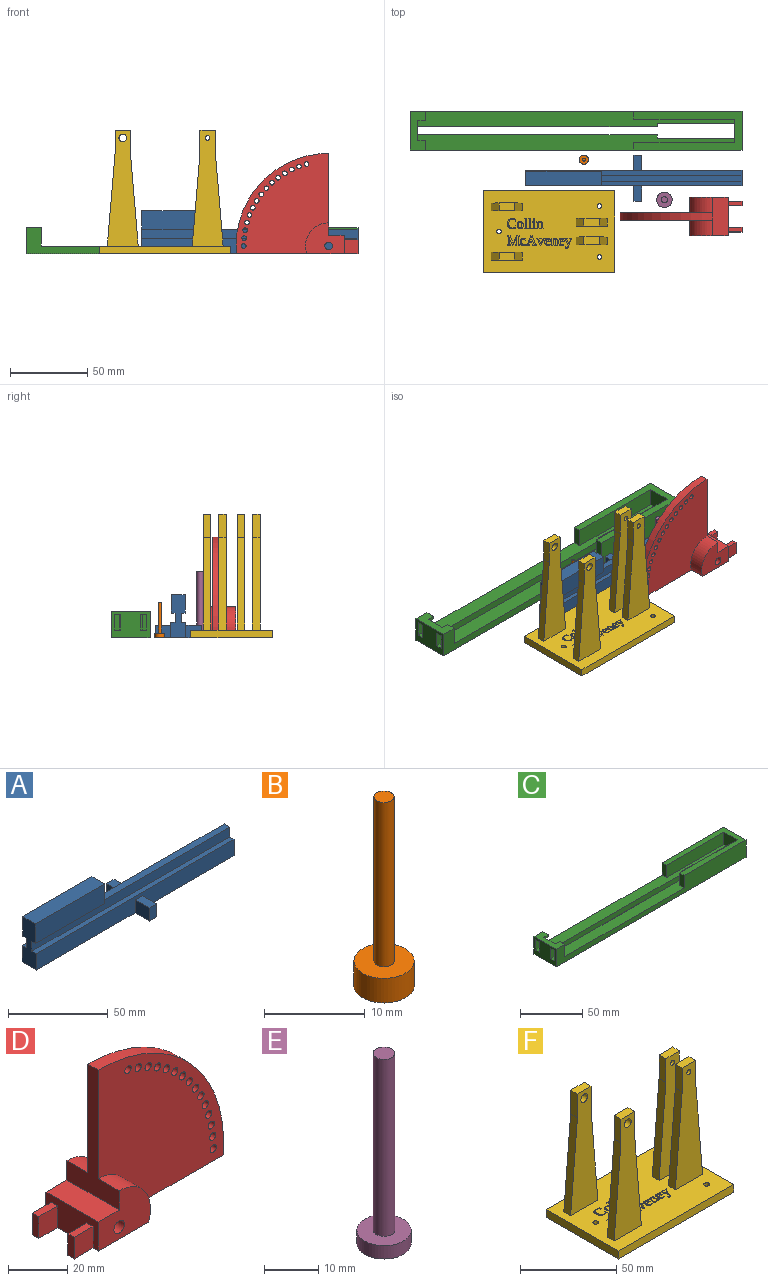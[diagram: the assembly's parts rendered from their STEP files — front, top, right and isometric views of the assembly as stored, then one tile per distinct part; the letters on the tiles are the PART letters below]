
ASSEMBLY  parts=6 mates=7
PART A: 28 faces, bbox 140x30x28 mm
  f0: plane 91x4mm, normal (0,0,1), area 364mm2, adj f11,f20,f21,f23
  f1: plane 140x3mm, normal (0,0,1), area 420mm2, adj f7,f11,f16,f21
  f2: plane 10x5.1mm, normal (0,0,1), area 51mm2, adj f4,f5,f6,f7
  f3: plane 10x5.1mm, normal (0,0,1), area 51mm2, adj f12,f13,f14,f15
  f4: plane 10x8mm, normal (-1,0,0), area 80mm2, adj f2,f5,f7,f17
  f5: plane 8x5.1mm, normal (0,-1,0), area 40.8mm2, adj f2,f4,f6,f17
  f6: plane 10x8mm, normal (1,0,0), area 80mm2, adj f2,f5,f7,f17
  f7: plane 140x10mm, normal (0,-1,0), area 1359.2mm2, adj f1,f2,f4,f6,f11,f16,f17
  f8: plane 138x8mm, normal (0,1,0), area 1104mm2, adj f9,f11,f17,f19
  f9: plane 8x2mm, normal (1,0,0), area 16mm2, adj f8,f10,f17,f19
  f10: plane 138x8mm, normal (0,-1,0), area 1104mm2, adj f9,f11,f17,f19
  f11: plane 16x10mm, normal (1,0,0), area 108mm2, adj f0,f1,f7,f8,f10,f15,f17,f18
  f12: plane 10x8mm, normal (1,0,0), area 80mm2, adj f3,f13,f15,f17
  f13: plane 8x5.1mm, normal (0,1,0), area 40.8mm2, adj f3,f12,f14,f17
  f14: plane 10x8mm, normal (-1,0,0), area 80mm2, adj f3,f13,f15,f17
  f15: plane 140x10mm, normal (0,1,0), area 1359.2mm2, adj f3,f11,f12,f14,f16,f17,f18
  f16: plane 28x10mm, normal (-1,0,0), area 232mm2, adj f1,f7,f15,f17,f18,f20,f21,f22
  f17: plane 140x30mm, normal (0,0,-1), area 1226mm2, adj f4,f5,f6,f7,f8,f9,f10,f11
  f18: plane 140x3mm, normal (0,0,1), area 420mm2, adj f11,f15,f16,f20
  f19: plane 138x2mm, normal (0,0,-1), area 276mm2, adj f8,f9,f10,f11
  f20: plane 140x6mm, normal (0,1,0), area 840mm2, adj f0,f11,f16,f18,f22
  f21: plane 140x6mm, normal (0,-1,0), area 840mm2, adj f0,f1,f11,f16,f27
  f22: plane 49x2.5mm, normal (0,0,-1), area 122.5mm2, adj f16,f20,f23,f24
  f23: plane 12x9mm, normal (1,0,0), area 108mm2, adj f0,f22,f24,f25,f26,f27
  f24: plane 49x12mm, normal (0,1,0), area 588mm2, adj f16,f22,f23,f26
  f25: plane 49x12mm, normal (0,-1,0), area 588mm2, adj f16,f23,f26,f27
  f26: plane 49x9mm, normal (0,0,1), area 441mm2, adj f16,f23,f24,f25
  f27: plane 49x2.5mm, normal (0,0,-1), area 122.5mm2, adj f16,f21,f23,f25
PART B: 5 faces, bbox 6x6x23 mm
  f0: cylinder r=3mm len=6mm, axis (0,0,-1), area 56.5mm2, adj f1,f2
  f1: plane 6x6mm, normal (0,0,1), area 25.1mm2, adj f0,f3
  f2: plane 6x6mm, normal (0,0,-1), area 28.3mm2, adj f0
  f3: cylinder r=1mm len=20mm, axis (0,0,-1), area 125.7mm2, adj f1,f4
  f4: plane 2x2mm, normal (0,0,1), area 3.1mm2, adj f3
PART C: 34 faces, bbox 215x25x17 mm
  f0: plane 210x10mm, normal (0,0,1), area 1610mm2, adj f1,f2,f5,f6,f7,f13,f16,f17
  f1: plane 25x17mm, normal (-1,0,0), area 345mm2, adj f0,f4,f12,f13,f18,f21,f22,f23
  f2: plane 12x6mm, normal (1,0,0), area 32mm2, adj f0,f13,f19,f21,f26,f27
  f3: plane 12x6mm, normal (1,0,0), area 32mm2, adj f4,f12,f20,f21,f23,f24
  f4: plane 210x10mm, normal (0,0,1), area 1610mm2, adj f1,f3,f7,f8,f9,f10,f12,f16
  f5: plane 5x2.5mm, normal (1,0,0), area 12.5mm2, adj f0,f6,f17,f18
  f6: plane 155x5mm, normal (0,1,0), area 775mm2, adj f0,f5,f7,f18
  f7: plane 17x13mm, normal (1,0,0), area 181mm2, adj f0,f4,f6,f8,f18,f19,f20,f21
  f8: plane 155x5mm, normal (0,-1,0), area 775mm2, adj f4,f7,f9,f18
  f9: plane 5x2.5mm, normal (1,0,0), area 12.5mm2, adj f4,f8,f10,f18
  f10: plane 50x5mm, normal (0,-1,0), area 250mm2, adj f4,f9,f16,f18
  f11: plane 7x5mm, normal (0,-1,0), area 35mm2, adj f14,f16,f18,f33
  f12: plane 215x17mm, normal (0,1,0), area 2035mm2, adj f1,f3,f4,f14,f18,f21,f28,f32
  f13: plane 215x17mm, normal (0,-1,0), area 2035mm2, adj f0,f1,f2,f14,f18,f21,f31,f32
  f14: plane 25x17mm, normal (1,0,0), area 390mm2, adj f11,f12,f13,f15,f18,f32,f33
  f15: plane 7x5mm, normal (0,1,0), area 35mm2, adj f14,f16,f18,f33
  f16: plane 17x15mm, normal (-1,0,0), area 195mm2, adj f0,f4,f10,f11,f15,f17,f18,f29
  f17: plane 50x5mm, normal (0,1,0), area 250mm2, adj f0,f5,f16,f18
  f18: plane 215x25mm, normal (0,0,-1), area 4075mm2, adj f1,f5,f6,f7,f8,f9,f10,f11
  f19: plane 5x2mm, normal (0,1,0), area 10mm2, adj f2,f7,f21,f26
  f20: plane 5x2mm, normal (0,-1,0), area 10mm2, adj f3,f7,f21,f23
  f21: plane 25x10mm, normal (0,0,1), area 185mm2, adj f1,f2,f3,f7,f12,f13,f19,f20
  f22: plane 10x5mm, normal (0,1,0), area 50mm2, adj f1,f4,f7,f23
  f23: plane 10x4mm, normal (0,0,-1), area 40mm2, adj f1,f3,f20,f22,f24
  f24: plane 10x10mm, normal (0,-1,0), area 100mm2, adj f1,f3,f4,f23
  f25: plane 10x5mm, normal (0,-1,0), area 50mm2, adj f0,f1,f7,f26
  f26: plane 10x4mm, normal (0,0,-1), area 40mm2, adj f1,f2,f19,f25,f27
  f27: plane 10x10mm, normal (0,1,0), area 100mm2, adj f0,f1,f2,f26
  f28: plane 12x5mm, normal (-1,0,0), area 60mm2, adj f4,f12,f29,f32
  f29: plane 65x12mm, normal (0,-1,0), area 780mm2, adj f4,f16,f28,f32
  f30: plane 65x12mm, normal (0,1,0), area 780mm2, adj f0,f16,f31,f32
  f31: plane 12x5mm, normal (-1,0,0), area 60mm2, adj f0,f13,f30,f32
  f32: plane 70x25mm, normal (0,0,1), area 775mm2, adj f12,f13,f14,f16,f28,f29,f30,f31
  f33: plane 5x5mm, normal (0,0,-1), area 25mm2, adj f11,f14,f15,f16
PART D: 35 faces, bbox 79x25x65 mm
  f0: plane 25x12mm, normal (-1,0,0), area 246mm2, adj f18,f19,f20,f22,f27,f28,f29,f31
  f1: plane 53x25mm, normal (-1,0,0), area 425mm2, adj f17,f18,f19,f22,f23,f24,f25,f26
  f2: cylinder r=1.5mm len=5mm, axis (0,1,0), area 47.1mm2, adj f24,f26
  f3: cylinder r=1.5mm len=5mm, axis (0,1,0), area 47.1mm2, adj f24,f26
  f4: cylinder r=1.5mm len=5mm, axis (0,1,0), area 47.1mm2, adj f24,f26
  f5: cylinder r=1.5mm len=5mm, axis (0,1,0), area 47.1mm2, adj f24,f26
  f6: cylinder r=1.5mm len=5mm, axis (0,1,0), area 47.1mm2, adj f24,f26
  f7: cylinder r=1.5mm len=5mm, axis (0,1,0), area 47.1mm2, adj f24,f26
  f8: cylinder r=1.5mm len=5mm, axis (0,1,0), area 47.1mm2, adj f24,f26
  f9: cylinder r=1.5mm len=5mm, axis (0,1,0), area 47.1mm2, adj f24,f26
  f10: cylinder r=1.5mm len=5mm, axis (0,1,0), area 47.1mm2, adj f24,f26
  f11: cylinder r=1.5mm len=5mm, axis (0,1,0), area 47.1mm2, adj f24,f26
  f12: cylinder r=1.5mm len=5mm, axis (0,1,0), area 47.1mm2, adj f24,f26
  f13: cylinder r=1.5mm len=5mm, axis (0,1,0), area 47.1mm2, adj f24,f26
  f14: cylinder r=1.5mm len=5mm, axis (0,1,0), area 47.1mm2, adj f24,f26
  f15: cylinder r=1.5mm len=5mm, axis (0,1,0), area 47.1mm2, adj f24,f26
  f16: cylinder r=1.5mm len=5mm, axis (0,1,0), area 47.1mm2, adj f24,f26
  f17: cylinder r=60mm len=65mm, axis (0,1,0), area 496.3mm2, adj f1,f20,f24,f26
  f18: plane 25x20mm, normal (0,-1,0), area 350.7mm2, adj f0,f1,f19,f20,f21,f23
  f19: plane 25x10mm, normal (0,0,1), area 250mm2, adj f0,f1,f18,f22
  f20: plane 78.79x25mm, normal (0,0,-1), area 885.8mm2, adj f0,f17,f18,f22,f23,f24,f25,f26
  f21: cylinder r=2.5mm len=25mm, axis (0,1,0), area 392.7mm2, adj f18,f22
  f22: plane 25x20mm, normal (0,1,0), area 350.7mm2, adj f0,f1,f19,f20,f21,f25
  f23: cylinder r=15mm len=20mm, axis (0,-1,0), area 286.6mm2, adj f1,f18,f20,f24
  f24: plane 65x60mm, normal (0,-1,0), area 2770.8mm2, adj f1,f2,f3,f4,f5,f6,f7,f8
  f25: cylinder r=15mm len=20mm, axis (0,1,0), area 286.6mm2, adj f1,f20,f22,f26
  f26: plane 65x60mm, normal (0,1,0), area 2770.8mm2, adj f1,f2,f3,f4,f5,f6,f7,f8
  f27: plane 9x3mm, normal (0,0,1), area 27mm2, adj f0,f28,f29,f30
  f28: plane 9x9mm, normal (0,1,0), area 81mm2, adj f0,f20,f27,f30
  f29: plane 9x9mm, normal (0,-1,0), area 81mm2, adj f0,f20,f27,f30
  f30: plane 9x3mm, normal (-1,0,0), area 27mm2, adj f20,f27,f28,f29
  f31: plane 9x9mm, normal (0,-1,0), area 81mm2, adj f0,f20,f32,f34
  f32: plane 9x3mm, normal (0,0,1), area 27mm2, adj f0,f31,f33,f34
  f33: plane 9x9mm, normal (0,1,0), area 81mm2, adj f0,f20,f32,f34
  f34: plane 9x3mm, normal (-1,0,0), area 27mm2, adj f20,f31,f32,f33
PART E: 5 faces, bbox 10x10x43 mm
  f0: cylinder r=5mm len=10mm, axis (0,0,-1), area 94.2mm2, adj f1,f2
  f1: plane 10x10mm, normal (0,0,1), area 66mm2, adj f0,f3
  f2: plane 10x10mm, normal (0,0,-1), area 78.5mm2, adj f0
  f3: cylinder r=2mm len=40mm, axis (0,0,-1), area 502.7mm2, adj f1,f4
  f4: plane 4x4mm, normal (0,0,1), area 12.6mm2, adj f3
PART F: 324 faces, bbox 85x53x80 mm
  f0: plane 85x53mm, normal (0,0,1), area 3956.6mm2, adj f5,f6,f7,f8,f10,f11,f13,f15
  f1: plane 15x5mm, normal (-1,0,0), area 75mm2, adj f10,f11,f12,f37
  f2: plane 15x5mm, normal (1,0,0), area 75mm2, adj f10,f11,f12,f36
  f3: plane 15x5mm, normal (-1,0,0), area 75mm2, adj f18,f19,f20,f35
  f4: plane 15x5mm, normal (1,0,0), area 75mm2, adj f18,f19,f20,f34
  f5: plane 85x5mm, normal (0,-1,0), area 425mm2, adj f0,f6,f8,f9
  f6: plane 53x5mm, normal (1,0,0), area 265mm2, adj f0,f5,f7,f9
  f7: plane 85x5mm, normal (0,1,0), area 425mm2, adj f0,f6,f8,f9
  f8: plane 53x5mm, normal (-1,0,0), area 265mm2, adj f0,f5,f7,f9
  f9: plane 85x53mm, normal (0,0,-1), area 4483.8mm2, adj f5,f6,f7,f8,f38,f39,f40
  f10: plane 75x20mm, normal (0,1,0), area 1030.4mm2, adj f0,f1,f2,f12,f29,f36,f37
  f11: plane 75x20mm, normal (0,-1,0), area 1030.4mm2, adj f0,f1,f2,f12,f29,f36,f37
  f12: plane 10x5mm, normal (0,0,1), area 50mm2, adj f1,f2,f10,f11
  f13: plane 75x20mm, normal (0,1,0), area 1030.4mm2, adj f0,f14,f16,f17,f28,f30,f31
  f14: plane 15x5mm, normal (-1,0,0), area 75mm2, adj f13,f15,f17,f30
  f15: plane 75x20mm, normal (0,-1,0), area 1030.4mm2, adj f0,f14,f16,f17,f28,f30,f31
  f16: plane 15x5mm, normal (1,0,0), area 75mm2, adj f13,f15,f17,f31
  f17: plane 10x5mm, normal (0,0,1), area 50mm2, adj f13,f14,f15,f16
  f18: plane 75x20mm, normal (0,1,0), area 1042.9mm2, adj f0,f3,f4,f20,f27,f34,f35
  f19: plane 75x20mm, normal (0,-1,0), area 1042.9mm2, adj f0,f3,f4,f20,f27,f34,f35
  f20: plane 10x5mm, normal (0,0,1), area 50mm2, adj f3,f4,f18,f19
  f21: plane 75x20mm, normal (0,1,0), area 1042.9mm2, adj f0,f22,f24,f25,f26,f32,f33
  f22: plane 15x5mm, normal (-1,0,0), area 75mm2, adj f21,f23,f25,f32
  f23: plane 75x20mm, normal (0,-1,0), area 1042.9mm2, adj f0,f22,f24,f25,f26,f32,f33
  f24: plane 15x5mm, normal (1,0,0), area 75mm2, adj f21,f23,f25,f33
  f25: plane 10x5mm, normal (0,0,1), area 50mm2, adj f21,f22,f23,f24
  f26: cylinder r=1.5mm len=5mm, axis (0,-1,0), area 47.1mm2, adj f21,f23
  f27: cylinder r=1.5mm len=5mm, axis (0,-1,0), area 47.1mm2, adj f18,f19
  f28: cylinder r=2.5mm len=5mm, axis (0,-1,0), area 78.5mm2, adj f13,f15
  f29: cylinder r=2.5mm len=5mm, axis (0,-1,0), area 78.5mm2, adj f10,f11
  f30: plane 60x5mm, normal (-1,0,0.08), area 301mm2, adj f0,f13,f14,f15
  f31: plane 60x5mm, normal (1,0,0.08), area 301mm2, adj f0,f13,f15,f16
  f32: plane 60x5mm, normal (-1,0,0.08), area 301mm2, adj f0,f21,f22,f23
  f33: plane 60x5mm, normal (1,0,0.08), area 301mm2, adj f0,f21,f23,f24
  f34: plane 60x5mm, normal (1,0,0.08), area 301mm2, adj f0,f4,f18,f19
  f35: plane 60x5mm, normal (-1,0,0.08), area 301mm2, adj f0,f3,f18,f19
  f36: plane 60x5mm, normal (1,0,0.08), area 301mm2, adj f0,f2,f10,f11
  f37: plane 60x5mm, normal (-1,0,0.08), area 301mm2, adj f0,f1,f10,f11
  f38: cylinder r=1.5mm len=5mm, axis (0,0,1), area 47.1mm2, adj f0,f9
  f39: cylinder r=1.5mm len=5mm, axis (0,0,1), area 47.1mm2, adj f0,f9
  f40: cylinder r=1.5mm len=5mm, axis (0,0,1), area 47.1mm2, adj f0,f9
  f41: extruded ~2.36x2mm, area 5.1mm2, adj f0,f42,f60,f61
  f42: extruded ~2.2x2mm, area 4.5mm2, adj f0,f41,f43,f61
  f43: plane 2x1.47mm, normal (-1,0.02,0), area 2.9mm2, adj f0,f42,f44,f61
  f44: plane 2x0.3mm, normal (0,-1,0), area 0.6mm2, adj f0,f43,f45,f61
  f45: plane 2x0.93mm, normal (0.98,-0.18,0), area 1.9mm2, adj f0,f44,f46,f61
  f46: extruded ~2x0.74mm, area 1.6mm2, adj f0,f45,f47,f61
  f47: extruded ~2x1mm, area 2mm2, adj f0,f46,f48,f61
  f48: extruded ~2x1.67mm, area 3.8mm2, adj f0,f47,f49,f61
  f49: extruded ~2.07x2mm, area 4.4mm2, adj f0,f48,f50,f61
  f50: extruded ~2.18x2mm, area 4.6mm2, adj f0,f49,f51,f61
  f51: extruded ~2x1.74mm, area 3.9mm2, adj f0,f50,f52,f61
  f52: extruded ~2x0.88mm, area 1.8mm2, adj f0,f51,f53,f61
  f53: extruded ~2x0.76mm, area 1.6mm2, adj f0,f52,f54,f61
  f54: plane 2x0.81mm, normal (0.99,0.17,0), area 1.6mm2, adj f0,f53,f55,f61
  f55: plane 2x0.31mm, normal (0,1,0), area 0.6mm2, adj f0,f54,f56,f61
  f56: plane 2x1.36mm, normal (-1,-0.02,0), area 2.7mm2, adj f0,f55,f57,f61
  f57: extruded ~2.09x2mm, area 4.2mm2, adj f0,f56,f58,f61
  f58: extruded ~2.41x2mm, area 5.2mm2, adj f0,f57,f59,f61
  f59: extruded ~2.43x2mm, area 5.3mm2, adj f0,f58,f60,f61
  f60: extruded ~2.31x2mm, area 5.1mm2, adj f0,f41,f59,f61
  f61: plane 6.4x5.44mm, normal (0,0,1), area 9.1mm2, adj f41,f42,f43,f44,f45,f46,f47,f48
  f62: extruded ~2x0.76mm, area 1.7mm2, adj f0,f63,f86,f87
  f63: plane 2x0.35mm, normal (-0.99,-0.12,0), area 0.7mm2, adj f0,f62,f64,f87
  f64: plane 2x1.25mm, normal (0,-1,0), area 2.5mm2, adj f0,f63,f65,f87
  f65: plane 2x0.21mm, normal (1,0,0), area 0.4mm2, adj f0,f64,f66,f87
  f66: plane 2x0.53mm, normal (0.22,0.98,0), area 1.1mm2, adj f0,f65,f67,f87
  f67: plane 3.72x2mm, normal (1,0,0), area 7.4mm2, adj f0,f66,f68,f87
  f68: plane 2x0.53mm, normal (0.22,-0.98,0), area 1.1mm2, adj f0,f67,f69,f87
  f69: plane 2x0.21mm, normal (1,0,0), area 0.4mm2, adj f0,f68,f70,f87
  f70: plane 2x1.89mm, normal (0,1,0), area 3.8mm2, adj f0,f69,f71,f87
  f71: plane 2x0.21mm, normal (-1,0,0), area 0.4mm2, adj f0,f70,f72,f87
  f72: plane 2x0.59mm, normal (-0.19,-0.98,0), area 1.2mm2, adj f0,f71,f73,f87
  f73: plane 3.48x2mm, normal (-1,0,0), area 7mm2, adj f0,f72,f74,f87
  f74: extruded ~2x1.03mm, area 2.1mm2, adj f0,f73,f75,f87
  f75: extruded ~2x0.58mm, area 1.3mm2, adj f0,f74,f76,f87
  f76: extruded ~2x0.61mm, area 1.3mm2, adj f0,f75,f77,f87
  f77: plane 2.79x2mm, normal (1,0,0), area 5.6mm2, adj f0,f76,f78,f87
  f78: plane 2x0.58mm, normal (0.2,-0.98,0), area 1.2mm2, adj f0,f77,f79,f87
  f79: plane 2x0.21mm, normal (1,0,0), area 0.4mm2, adj f0,f78,f80,f87
  f80: plane 2x1.88mm, normal (0,1,0), area 3.8mm2, adj f0,f79,f81,f87
  f81: plane 2x0.21mm, normal (-1,0,0), area 0.4mm2, adj f0,f80,f82,f87
  f82: plane 2x0.53mm, normal (-0.21,-0.98,0), area 1.1mm2, adj f0,f81,f83,f87
  f83: plane 2.87x2mm, normal (-1,0,0), area 5.7mm2, adj f0,f82,f84,f87
  f84: extruded ~2x0.96mm, area 2mm2, adj f0,f83,f85,f87
  f85: extruded ~2x0.86mm, area 1.9mm2, adj f0,f84,f86,f87
  f86: extruded ~2x0.67mm, area 1.4mm2, adj f0,f62,f85,f87
  f87: plane 4.49x4.4mm, normal (0,0,1), area 8.2mm2, adj f62,f63,f64,f65,f66,f67,f68,f69
  f88: extruded ~2x0.72mm, area 1.4mm2, adj f0,f89,f112,f113
  f89: extruded ~2x0.62mm, area 1.3mm2, adj f0,f88,f90,f113
  f90: extruded ~2x0.51mm, area 1.4mm2, adj f0,f89,f91,f113
  f91: extruded ~2x1.1mm, area 2.4mm2, adj f0,f90,f92,f113
  f92: plane 4.34x2mm, normal (-0.93,0.37,0), area 9.3mm2, adj f0,f91,f93,f113
  f93: plane 2x0.46mm, normal (-0.21,0.98,0), area 0.9mm2, adj f0,f92,f94,f113
  f94: plane 2x0.21mm, normal (-1,0,0), area 0.4mm2, adj f0,f93,f95,f113
  f95: plane 2x1.63mm, normal (0,-1,0), area 3.3mm2, adj f0,f94,f96,f113
  f96: plane 2x0.21mm, normal (1,0,0), area 0.4mm2, adj f0,f95,f97,f113
  f97: plane 2x0.68mm, normal (0.17,0.99,0), area 1.4mm2, adj f0,f96,f98,f113
  f98: plane 3.07x2mm, normal (0.94,-0.35,0), area 6.5mm2, adj f0,f97,f99,f113
  f99: plane 3.06x2mm, normal (-0.93,-0.36,0), area 6.6mm2, adj f0,f98,f100,f113
  f100: plane 2x0.69mm, normal (-0.18,0.98,0), area 1.4mm2, adj f0,f99,f101,f113
  f101: plane 2x0.21mm, normal (-1,0,0), area 0.4mm2, adj f0,f100,f102,f113
  f102: plane 2.03x2mm, normal (0,-1,0), area 4.1mm2, adj f0,f101,f103,f113
  f103: plane 2x0.21mm, normal (1,0,0), area 0.4mm2, adj f0,f102,f104,f113
  f104: plane 2x0.45mm, normal (0.25,0.97,0), area 0.9mm2, adj f0,f103,f105,f113
  f105: plane 4.09x2mm, normal (0.93,0.38,0), area 8.8mm2, adj f0,f104,f106,f113
  f106: extruded ~2x0.98mm, area 2.1mm2, adj f0,f105,f107,f113
  f107: extruded ~2x0.41mm, area 1.1mm2, adj f0,f106,f108,f113
  f108: extruded ~2x0.45mm, area 1mm2, adj f0,f107,f109,f113
  f109: extruded ~2x0.4mm, area 0.8mm2, adj f0,f108,f110,f113
  f110: plane 2x0.45mm, normal (-0.95,-0.32,0), area 0.9mm2, adj f0,f109,f111,f113
  f111: plane 2x0.22mm, normal (0,-1,0), area 0.4mm2, adj f0,f110,f112,f113
  f112: plane 2x0.94mm, normal (1,0,0), area 1.9mm2, adj f0,f88,f111,f113
  f113: plane 6.43x4.61mm, normal (0,0,1), area 7.4mm2, adj f88,f89,f90,f91,f92,f93,f94,f95
  f114: extruded ~2x1.46mm, area 3mm2, adj f115,f128,f129,f320
  f115: extruded ~2x1.48mm, area 3.1mm2, adj f114,f116,f129,f320
  f116: extruded ~2x0.91mm, area 2.1mm2, adj f115,f117,f129,f320
  f117: extruded ~2x0.88mm, area 2.1mm2, adj f116,f118,f129,f320
  f118: extruded ~2x1.49mm, area 3.1mm2, adj f117,f119,f129,f320
  f119: extruded ~2x1.47mm, area 3mm2, adj f118,f120,f129,f320
  f120: extruded ~2x0.88mm, area 2.1mm2, adj f119,f128,f129,f320
  f121: extruded ~2.3x2.05mm, area 7.1mm2, adj f0,f122,f127,f129
  f122: extruded ~2x1.71mm, area 3.6mm2, adj f0,f121,f123,f129
  f123: extruded ~2x1.5mm, area 3.3mm2, adj f0,f122,f124,f129
  f124: extruded ~2x1.52mm, area 3.4mm2, adj f0,f123,f125,f129
  f125: extruded ~2x1.69mm, area 3.6mm2, adj f0,f124,f126,f129
  f126: extruded ~2x1.71mm, area 3.6mm2, adj f0,f125,f127,f129
  f127: extruded ~2x1.49mm, area 3.3mm2, adj f0,f121,f126,f129
  f128: extruded ~2x0.92mm, area 2.1mm2, adj f114,f120,f129,f320
  f129: plane 4.58x4.04mm, normal (0,0,1), area 7.7mm2, adj f114,f115,f116,f117,f118,f119,f120,f121
  f130: plane 3.03x2mm, normal (-0.94,0.33,0), area 6.4mm2, adj f131,f148,f149,f321
  f131: plane 3.03x2mm, normal (0.94,0.34,0), area 6.4mm2, adj f130,f148,f149,f321
  f132: plane 2x0.25mm, normal (-1,0,0), area 0.5mm2, adj f0,f133,f147,f149
  f133: plane 2x0.84mm, normal (-0.15,-0.99,0), area 1.7mm2, adj f0,f132,f134,f149
  f134: plane 2x1.8mm, normal (-0.94,0.33,0), area 3.8mm2, adj f0,f133,f135,f149
  f135: plane 2.46x2mm, normal (0,1,0), area 4.9mm2, adj f0,f134,f136,f149
  f136: plane 2x1.8mm, normal (0.95,0.33,0), area 3.8mm2, adj f0,f135,f137,f149
  f137: plane 2x0.84mm, normal (0.15,-0.99,0), area 1.7mm2, adj f0,f136,f138,f149
  f138: plane 2x0.25mm, normal (1,0,0), area 0.5mm2, adj f0,f137,f139,f149
  f139: plane 2.64x2mm, normal (0,1,0), area 5.3mm2, adj f0,f138,f140,f149
  f140: plane 2x0.25mm, normal (-1,0,0), area 0.5mm2, adj f0,f139,f141,f149
  f141: plane 2x0.79mm, normal (-0.16,-0.99,0), area 1.6mm2, adj f0,f140,f142,f149
  f142: plane 5.92x2.21mm, normal (-0.94,-0.35,0), area 12.6mm2, adj f0,f141,f143,f149
  f143: plane 2x0.88mm, normal (0,-1,0), area 1.8mm2, adj f0,f142,f144,f149
  f144: plane 5.92x2.13mm, normal (0.94,-0.34,0), area 12.6mm2, adj f0,f143,f145,f149
  f145: plane 2x0.71mm, normal (0.17,-0.98,0), area 1.4mm2, adj f0,f144,f146,f149
  f146: plane 2x0.25mm, normal (1,0,0), area 0.5mm2, adj f0,f145,f147,f149
  f147: plane 2.05x2mm, normal (0,1,0), area 4.1mm2, adj f0,f132,f146,f149
  f148: plane 2.17x2mm, normal (0,-1,0), area 4.3mm2, adj f130,f131,f149,f321
  f149: plane 6.71x6.29mm, normal (0,0,1), area 10.8mm2, adj f130,f131,f132,f133,f134,f135,f136,f137
  f150: extruded ~2x0.74mm, area 1.8mm2, adj f151,f170,f171,f322
  f151: extruded ~2x0.66mm, area 1.6mm2, adj f150,f152,f171,f322
  f152: extruded ~2x1.19mm, area 2.4mm2, adj f151,f153,f171,f322
  f153: plane 2x1.87mm, normal (0,-1,0), area 3.7mm2, adj f152,f170,f171,f322
  f154: plane 2x0.08mm, normal (-1,0,0), area 0.2mm2, adj f0,f155,f169,f171
  f155: plane 2.69x2mm, normal (0,1,0), area 5.4mm2, adj f0,f154,f156,f171
  f156: plane 2x0.38mm, normal (-1,0,0), area 0.8mm2, adj f0,f155,f157,f171
  f157: extruded ~2x1.91mm, area 5.8mm2, adj f0,f156,f158,f171
  f158: extruded ~2x1.37mm, area 3.1mm2, adj f0,f157,f159,f171
  f159: extruded ~2x1.71mm, area 3.6mm2, adj f0,f158,f160,f171
  f160: extruded ~2x1.76mm, area 3.7mm2, adj f0,f159,f161,f171
  f161: extruded ~2x1.49mm, area 3.3mm2, adj f0,f160,f162,f171
  f162: extruded ~2x0.78mm, area 1.6mm2, adj f0,f161,f163,f171
  f163: extruded ~2x0.61mm, area 1.3mm2, adj f0,f162,f164,f171
  f164: plane 2x0.26mm, normal (-1,0,0), area 0.5mm2, adj f0,f163,f165,f171
  f165: extruded ~2x0.57mm, area 1.1mm2, adj f0,f164,f166,f171
  f166: extruded ~2x0.6mm, area 1.2mm2, adj f0,f165,f167,f171
  f167: extruded ~2x0.77mm, area 1.6mm2, adj f0,f166,f168,f171
  f168: extruded ~2x0.54mm, area 1.4mm2, adj f0,f167,f169,f171
  f169: extruded ~2x1mm, area 2mm2, adj f0,f154,f168,f171
  f170: extruded ~2x1.15mm, area 2.4mm2, adj f150,f153,f171,f322
  f171: plane 4.58x3.53mm, normal (0,0,1), area 7.1mm2, adj f150,f151,f152,f153,f154,f155,f156,f157
  f172: extruded ~2x0.74mm, area 1.8mm2, adj f173,f192,f193,f323
  f173: extruded ~2x0.66mm, area 1.6mm2, adj f172,f174,f193,f323
  f174: extruded ~2x1.19mm, area 2.4mm2, adj f173,f175,f193,f323
  f175: plane 2x1.87mm, normal (0,-1,0), area 3.7mm2, adj f174,f192,f193,f323
  f176: plane 2x0.08mm, normal (-1,0,0), area 0.2mm2, adj f0,f177,f191,f193
  f177: plane 2.69x2mm, normal (0,1,0), area 5.4mm2, adj f0,f176,f178,f193
  f178: plane 2x0.38mm, normal (-1,0,0), area 0.8mm2, adj f0,f177,f179,f193
  f179: extruded ~2x1.91mm, area 5.8mm2, adj f0,f178,f180,f193
  f180: extruded ~2x1.37mm, area 3.1mm2, adj f0,f179,f181,f193
  f181: extruded ~2x1.71mm, area 3.6mm2, adj f0,f180,f182,f193
  f182: extruded ~2x1.76mm, area 3.7mm2, adj f0,f181,f183,f193
  f183: extruded ~2x1.49mm, area 3.3mm2, adj f0,f182,f184,f193
  f184: extruded ~2x0.78mm, area 1.6mm2, adj f0,f183,f185,f193
  f185: extruded ~2x0.61mm, area 1.3mm2, adj f0,f184,f186,f193
  f186: plane 2x0.26mm, normal (-1,0,0), area 0.5mm2, adj f0,f185,f187,f193
  f187: extruded ~2x0.57mm, area 1.1mm2, adj f0,f186,f188,f193
  f188: extruded ~2x0.6mm, area 1.2mm2, adj f0,f187,f189,f193
  f189: extruded ~2x0.77mm, area 1.6mm2, adj f0,f188,f190,f193
  f190: extruded ~2x0.54mm, area 1.4mm2, adj f0,f189,f191,f193
  f191: extruded ~2x1mm, area 2mm2, adj f0,f176,f190,f193
  f192: extruded ~2x1.15mm, area 2.4mm2, adj f172,f175,f193,f323
  f193: plane 4.58x3.53mm, normal (0,0,1), area 7.1mm2, adj f172,f173,f174,f175,f176,f177,f178,f179
  f194: plane 2x0.75mm, normal (-0.15,-0.99,0), area 1.5mm2, adj f0,f195,f203,f204
  f195: plane 6.28x2mm, normal (-1,0,0), area 12.6mm2, adj f0,f194,f196,f204
  f196: plane 2x1.52mm, normal (0,-1,0), area 3mm2, adj f0,f195,f197,f204
  f197: plane 2x0.21mm, normal (1,0,0), area 0.4mm2, adj f0,f196,f198,f204
  f198: plane 2x0.74mm, normal (0.15,0.99,0), area 1.5mm2, adj f0,f197,f199,f204
  f199: plane 5.96x2mm, normal (1,0,0), area 11.9mm2, adj f0,f198,f200,f204
  f200: plane 2x0.74mm, normal (0.15,-0.99,0), area 1.5mm2, adj f0,f199,f201,f204
  f201: plane 2x0.21mm, normal (1,0,0), area 0.4mm2, adj f0,f200,f202,f204
  f202: plane 2.27x2mm, normal (0,1,0), area 4.5mm2, adj f0,f201,f203,f204
  f203: plane 2x0.21mm, normal (-1,0,0), area 0.4mm2, adj f0,f194,f202,f204
  f204: plane 6.61x2.27mm, normal (0,0,1), area 5.7mm2, adj f194,f195,f196,f197,f198,f199,f200,f201
  f205: plane 2x0.75mm, normal (-0.15,-0.99,0), area 1.5mm2, adj f0,f206,f214,f215
  f206: plane 6.28x2mm, normal (-1,0,0), area 12.6mm2, adj f0,f205,f207,f215
  f207: plane 2x1.52mm, normal (0,-1,0), area 3mm2, adj f0,f206,f208,f215
  f208: plane 2x0.21mm, normal (1,0,0), area 0.4mm2, adj f0,f207,f209,f215
  f209: plane 2x0.74mm, normal (0.15,0.99,0), area 1.5mm2, adj f0,f208,f210,f215
  f210: plane 5.96x2mm, normal (1,0,0), area 11.9mm2, adj f0,f209,f211,f215
  f211: plane 2x0.74mm, normal (0.15,-0.99,0), area 1.5mm2, adj f0,f210,f212,f215
  f212: plane 2x0.21mm, normal (1,0,0), area 0.4mm2, adj f0,f211,f213,f215
  f213: plane 2.27x2mm, normal (0,1,0), area 4.5mm2, adj f0,f212,f214,f215
  f214: plane 2x0.21mm, normal (-1,0,0), area 0.4mm2, adj f0,f205,f213,f215
  f215: plane 6.61x2.27mm, normal (0,0,1), area 5.7mm2, adj f205,f206,f207,f208,f209,f210,f211,f212
  f216: extruded ~2x0.35mm, area 0.8mm2, adj f0,f217,f223,f224
  f217: extruded ~2x0.36mm, area 0.8mm2, adj f0,f216,f218,f224
  f218: extruded ~2x0.36mm, area 0.8mm2, adj f0,f217,f219,f224
  f219: extruded ~2x0.35mm, area 0.8mm2, adj f0,f218,f220,f224
  f220: extruded ~2x0.36mm, area 0.8mm2, adj f0,f219,f221,f224
  f221: extruded ~2x0.35mm, area 0.8mm2, adj f0,f220,f222,f224
  f222: extruded ~2x0.35mm, area 0.8mm2, adj f0,f221,f223,f224
  f223: extruded ~2x0.36mm, area 0.8mm2, adj f0,f216,f222,f224
  f224: plane 1.01x1.01mm, normal (0,0,1), area 0.8mm2, adj f216,f217,f218,f219,f220,f221,f222,f223
  f225: plane 2x0.75mm, normal (-0.15,-0.99,0), area 1.5mm2, adj f0,f226,f234,f235
  f226: plane 4.05x2mm, normal (-1,0,0), area 8.1mm2, adj f0,f225,f227,f235
  f227: plane 2x1.39mm, normal (0,-1,0), area 2.8mm2, adj f0,f226,f228,f235
  f228: plane 2x0.21mm, normal (1,0,0), area 0.4mm2, adj f0,f227,f229,f235
  f229: plane 2x0.62mm, normal (0.18,0.98,0), area 1.3mm2, adj f0,f228,f230,f235
  f230: plane 3.72x2mm, normal (1,0,0), area 7.4mm2, adj f0,f229,f231,f235
  f231: plane 2x0.74mm, normal (0.15,-0.99,0), area 1.5mm2, adj f0,f230,f232,f235
  f232: plane 2x0.21mm, normal (1,0,0), area 0.4mm2, adj f0,f231,f233,f235
  f233: plane 2.27x2mm, normal (0,1,0), area 4.5mm2, adj f0,f232,f234,f235
  f234: plane 2x0.21mm, normal (-1,0,0), area 0.4mm2, adj f0,f225,f233,f235
  f235: plane 4.37x2.27mm, normal (0,0,1), area 3.9mm2, adj f225,f226,f227,f228,f229,f230,f231,f232
  f236: plane 2x0.35mm, normal (0,1,0), area 0.7mm2, adj f0,f237,f250,f251
  f237: plane 4.16x2mm, normal (-0.92,0.39,0), area 9mm2, adj f0,f236,f238,f251
  f238: plane 2x0.42mm, normal (-0.23,0.97,0), area 0.9mm2, adj f0,f237,f239,f251
  f239: plane 2x0.21mm, normal (-1,0,0), area 0.4mm2, adj f0,f238,f240,f251
  f240: plane 2x1.62mm, normal (0,-1,0), area 3.2mm2, adj f0,f239,f241,f251
  f241: plane 2x0.21mm, normal (1,0,0), area 0.4mm2, adj f0,f240,f242,f251
  f242: plane 2x0.69mm, normal (0.17,0.99,0), area 1.4mm2, adj f0,f241,f243,f251
  f243: plane 3.03x2mm, normal (0.93,-0.37,0), area 6.5mm2, adj f0,f242,f244,f251
  f244: plane 3.02x2mm, normal (-0.92,-0.39,0), area 6.6mm2, adj f0,f243,f245,f251
  f245: plane 2x0.69mm, normal (-0.18,0.98,0), area 1.4mm2, adj f0,f244,f246,f251
  f246: plane 2x0.21mm, normal (-1,0,0), area 0.4mm2, adj f0,f245,f247,f251
  f247: plane 2.04x2mm, normal (0,-1,0), area 4.1mm2, adj f0,f246,f248,f251
  f248: plane 2x0.21mm, normal (1,0,0), area 0.4mm2, adj f0,f247,f249,f251
  f249: plane 2x0.45mm, normal (0.25,0.97,0), area 0.9mm2, adj f0,f248,f250,f251
  f250: plane 4.14x2mm, normal (0.92,0.4,0), area 9mm2, adj f0,f236,f249,f251
  f251: plane 4.76x4.47mm, normal (0,0,1), area 6mm2, adj f236,f237,f238,f239,f240,f241,f242,f243
  f252: extruded ~2x0.63mm, area 1.4mm2, adj f0,f253,f266,f267
  f253: plane 2x0.28mm, normal (-1,0,0), area 0.6mm2, adj f0,f252,f254,f267
  f254: extruded ~2x1.18mm, area 2.4mm2, adj f0,f253,f255,f267
  f255: extruded ~2x1.17mm, area 2.6mm2, adj f0,f254,f256,f267
  f256: extruded ~2x1.41mm, area 3mm2, adj f0,f255,f257,f267
  f257: extruded ~2x1.9mm, area 5.1mm2, adj f0,f256,f258,f267
  f258: extruded ~2x0.93mm, area 1.9mm2, adj f0,f257,f259,f267
  f259: plane 2x0.77mm, normal (0.97,0.25,0), area 1.6mm2, adj f0,f258,f260,f267
  f260: plane 2x0.26mm, normal (0,1,0), area 0.5mm2, adj f0,f259,f261,f267
  f261: plane 2x1.22mm, normal (-1,0,0), area 2.4mm2, adj f0,f260,f262,f267
  f262: extruded ~2x1.37mm, area 2.8mm2, adj f0,f261,f263,f267
  f263: extruded ~2x1.55mm, area 3.4mm2, adj f0,f262,f264,f267
  f264: extruded ~2x1.68mm, area 3.6mm2, adj f0,f263,f265,f267
  f265: extruded ~2.31x2.13mm, area 7.2mm2, adj f0,f264,f266,f267
  f266: extruded ~2x0.82mm, area 1.7mm2, adj f0,f252,f265,f267
  f267: plane 4.58x3.57mm, normal (0,0,1), area 5.6mm2, adj f252,f253,f254,f255,f256,f257,f258,f259
  f268: plane 2x0.16mm, normal (0,1,0), area 0.3mm2, adj f0,f269,f292,f293
  f269: plane 5.36x2.49mm, normal (-0.91,0.42,0), area 11.8mm2, adj f0,f268,f270,f293
  f270: plane 4.99x2mm, normal (1,0,0), area 10mm2, adj f0,f269,f271,f293
  f271: plane 2x0.84mm, normal (0.15,-0.99,0), area 1.7mm2, adj f0,f270,f272,f293
  f272: plane 2x0.25mm, normal (1,0,0), area 0.5mm2, adj f0,f271,f273,f293
  f273: plane 2.53x2mm, normal (0,1,0), area 5.1mm2, adj f0,f272,f274,f293
  f274: plane 2x0.25mm, normal (-1,0,0), area 0.5mm2, adj f0,f273,f275,f293
  f275: plane 2x0.8mm, normal (-0.15,-0.99,0), area 1.6mm2, adj f0,f274,f276,f293
  f276: plane 5.5x2mm, normal (-1,0,0), area 11mm2, adj f0,f275,f277,f293
  f277: plane 2x0.8mm, normal (-0.15,0.99,0), area 1.6mm2, adj f0,f276,f278,f293
  f278: plane 2x0.25mm, normal (-1,0,0), area 0.5mm2, adj f0,f277,f279,f293
  f279: plane 2x1.79mm, normal (0,-1,0), area 3.6mm2, adj f0,f278,f280,f293
  f280: plane 4.74x2.21mm, normal (0.91,-0.42,0), area 10.5mm2, adj f0,f279,f281,f293
  f281: plane 4.74x2.03mm, normal (-0.92,-0.39,0), area 10.3mm2, adj f0,f280,f282,f293
  f282: plane 2x1.89mm, normal (0,-1,0), area 3.8mm2, adj f0,f281,f283,f293
  f283: plane 2x0.25mm, normal (1,0,0), area 0.5mm2, adj f0,f282,f284,f293
  f284: plane 2x0.8mm, normal (0.15,0.99,0), area 1.6mm2, adj f0,f283,f285,f293
  f285: plane 5.5x2mm, normal (1,0,0), area 11mm2, adj f0,f284,f286,f293
  f286: plane 2x0.8mm, normal (0.15,-0.99,0), area 1.6mm2, adj f0,f285,f287,f293
  f287: plane 2x0.25mm, normal (1,0,0), area 0.5mm2, adj f0,f286,f288,f293
  f288: plane 2.13x2mm, normal (0,1,0), area 4.3mm2, adj f0,f287,f289,f293
  f289: plane 2x0.25mm, normal (-1,0,0), area 0.5mm2, adj f0,f288,f290,f293
  f290: plane 2x0.84mm, normal (-0.15,-0.99,0), area 1.7mm2, adj f0,f289,f291,f293
  f291: plane 4.99x2mm, normal (-1,0,0), area 10mm2, adj f0,f290,f292,f293
  f292: plane 5.36x2.28mm, normal (0.92,0.39,0), area 11.7mm2, adj f0,f268,f291,f293
  f293: plane 7.92x6.24mm, normal (0,0,1), area 18mm2, adj f268,f269,f270,f271,f272,f273,f274,f275
  f294: extruded ~2x0.76mm, area 1.7mm2, adj f0,f295,f318,f319
  f295: plane 2x0.35mm, normal (-0.99,-0.12,0), area 0.7mm2, adj f0,f294,f296,f319
  f296: plane 2x1.25mm, normal (0,-1,0), area 2.5mm2, adj f0,f295,f297,f319
  f297: plane 2x0.21mm, normal (1,0,0), area 0.4mm2, adj f0,f296,f298,f319
  f298: plane 2x0.53mm, normal (0.22,0.98,0), area 1.1mm2, adj f0,f297,f299,f319
  f299: plane 3.72x2mm, normal (1,0,0), area 7.4mm2, adj f0,f298,f300,f319
  f300: plane 2x0.53mm, normal (0.22,-0.98,0), area 1.1mm2, adj f0,f299,f301,f319
  f301: plane 2x0.21mm, normal (1,0,0), area 0.4mm2, adj f0,f300,f302,f319
  f302: plane 2x1.89mm, normal (0,1,0), area 3.8mm2, adj f0,f301,f303,f319
  f303: plane 2x0.21mm, normal (-1,0,0), area 0.4mm2, adj f0,f302,f304,f319
  f304: plane 2x0.59mm, normal (-0.19,-0.98,0), area 1.2mm2, adj f0,f303,f305,f319
  f305: plane 3.48x2mm, normal (-1,0,0), area 7mm2, adj f0,f304,f306,f319
  f306: extruded ~2x1.03mm, area 2.1mm2, adj f0,f305,f307,f319
  f307: extruded ~2x0.58mm, area 1.3mm2, adj f0,f306,f308,f319
  f308: extruded ~2x0.61mm, area 1.3mm2, adj f0,f307,f309,f319
  f309: plane 2.79x2mm, normal (1,0,0), area 5.6mm2, adj f0,f308,f310,f319
  f310: plane 2x0.58mm, normal (0.2,-0.98,0), area 1.2mm2, adj f0,f309,f311,f319
  f311: plane 2x0.21mm, normal (1,0,0), area 0.4mm2, adj f0,f310,f312,f319
  f312: plane 2x1.88mm, normal (0,1,0), area 3.8mm2, adj f0,f311,f313,f319
  f313: plane 2x0.21mm, normal (-1,0,0), area 0.4mm2, adj f0,f312,f314,f319
  f314: plane 2x0.53mm, normal (-0.21,-0.98,0), area 1.1mm2, adj f0,f313,f315,f319
  f315: plane 2.87x2mm, normal (-1,0,0), area 5.7mm2, adj f0,f314,f316,f319
  f316: extruded ~2x0.96mm, area 2mm2, adj f0,f315,f317,f319
  f317: extruded ~2x0.86mm, area 1.9mm2, adj f0,f316,f318,f319
  f318: extruded ~2x0.67mm, area 1.4mm2, adj f0,f294,f317,f319
  f319: plane 4.49x4.4mm, normal (0,0,1), area 8.2mm2, adj f294,f295,f296,f297,f298,f299,f300,f301
  f320: plane 3.84x2.36mm, normal (0,0,1), area 7.7mm2, adj f114,f115,f116,f117,f118,f119,f120,f128
  f321: plane 3.03x2.17mm, normal (0,0,1), area 3.3mm2, adj f130,f131,f148
  f322: plane 1.87x1.54mm, normal (0,0,1), area 2.4mm2, adj f150,f151,f152,f153,f170
  f323: plane 1.87x1.54mm, normal (0,0,1), area 2.4mm2, adj f172,f173,f174,f175,f192
PLACE A t=(0,-13.24,0)mm
PLACE B t=(-46.78,-58.93,0)mm
PLACE C at identity fixed
PLACE D rot(axis=(0,0,-1),180deg) t=(-19,-55.57,5)mm
PLACE E t=(-6.89,-73.17,0)mm
PLACE F t=(-82.35,-79.35,0)mm
MATE planar A.f17 <-> C.f18  axis (0,0,-1) through (-138,-17.24,0)mm
MATE planar E.f0 <-> C.f18  axis (0,0,-1) through (-50.28,-32.27,0)mm
MATE planar A.f11 <-> C.f14  axis (1,0,0) through (0,-18.24,6.93)mm
MATE planar F.f9 <-> A.f17  axis (0,0,-1) through (-124.9,-52.85,0)mm
MATE planar B.f0 <-> C.f18  axis (0,0,-1) through (-102.42,-6.21,0)mm
MATE planar A.f11 <-> D.f30  axis (1,0,0) through (0,-18.24,6.93)mm
MATE planar F.f9 <-> D.f20  axis (0,0,-1) through (-124.9,-52.85,0)mm
